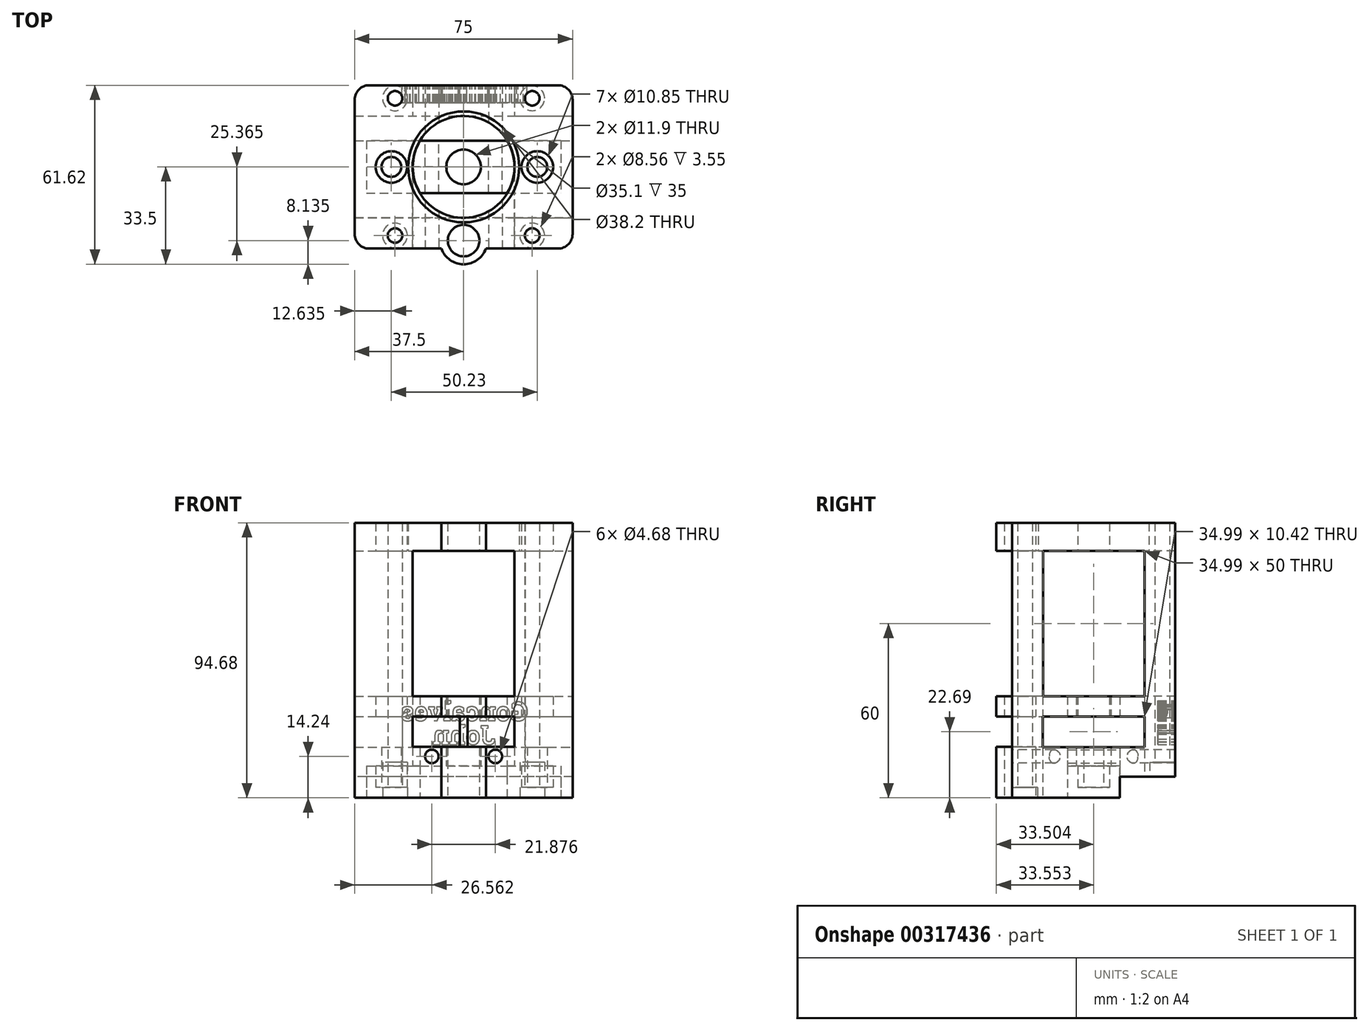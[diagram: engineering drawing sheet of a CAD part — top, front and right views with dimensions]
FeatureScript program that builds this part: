
annotation { "Feature Type Name" : "Feature", "Feature Type Description" : "" }
export const myFeature = defineFeature(function(context is Context, id is Id, definition is map)
    precondition{}
    {
        {
            var Q0;
            Q0=qCreatedBy(makeId("Top.planeOp"),FACE);
            var sketch = newSketch(context, id + "F0", { "sketchPlane" : qUnion([Q0])});
            skLineSegment(sketch, "E0.bottom", {"start": v(-33.5, 9.05) * mm, "end": v(33.5, 9.05) * mm});
            skLineSegment(sketch, "E0.top", {"start": v(-33.5, -9.05) * mm, "end": v(33.5, -9.05) * mm});
            skLineSegment(sketch, "E0.left", {"start": v(-33.5, 9.05) * mm, "end": v(-33.5, -9.05) * mm});
            skLineSegment(sketch, "E0.right", {"start": v(33.5, 9.05) * mm, "end": v(33.5, -9.05) * mm});
            skCircle(sketch, "E1", {"center": v(0, 0) * mm, "radius": 5.95 * mm});
            skCircle(sketch, "E2", {"center": v(25.37, 0) * mm, "radius": 3.42 * mm});
            skCircle(sketch, "E3", {"center": v(-24.87, 0) * mm, "radius": 3.42 * mm});
            skLineSegment(sketch, "E4.bottom", {"start": v(-14.98, 9.05) * mm, "end": v(14.98, 9.05) * mm});
            skLineSegment(sketch, "E4.top", {"start": v(-14.98, -9.05) * mm, "end": v(14.98, -9.05) * mm});
            skLineSegment(sketch, "E4.left", {"start": v(-14.98, 9.05) * mm, "end": v(-14.98, -9.05) * mm});
            skLineSegment(sketch, "E4.right", {"start": v(14.98, 9.05) * mm, "end": v(14.98, -9.05) * mm});
            skCircle(sketch, "E5", {"center": v(-24.87, 0) * mm, "radius": 5.42 * mm});
            skCircle(sketch, "E6", {"center": v(25.37, 0) * mm, "radius": 5.42 * mm});
            skCircle(sketch, "E7", {"center": v(0, 0) * mm, "radius": 17.5 * mm});
            skSolve(sketch);
        }
        {
            var Q0;
            Q0=makeQuery(id+"F0.imprint","IMPRINT",FACE,{"disambiguationData":[TD([[makeQuery(id+"F0.imprint","IMPRINT",EDGE,{"derivedFrom":sQuery(id+"F0.wireOp",EDGE,"E1")}),-1.0]])]});
            var Q1;
            {var subQ0=sQuery(id+"F0.wireOp",EDGE,"E4.left");Q1=makeQuery(id+"F0.imprint","IMPRINT",FACE,{"disambiguationData":[TD([[makeQuery(id+"F0.imprint","IMPRINT",EDGE,{"derivedFrom":subQ0}),-1.0]])]});}
            var Q2;
            {var subQ0=sQuery(id+"F0.wireOp",EDGE,"E4.right");Q2=makeQuery(id+"F0.imprint","IMPRINT",FACE,{"disambiguationData":[TD([[makeQuery(id+"F0.imprint","IMPRINT",EDGE,{"derivedFrom":subQ0}),1.0]])]});}
            extrude(context, id + "F1", {"entities" : qUnion([Q0, Q1, Q2]), "offsetDistance" : 25 * mm, "depth" : 28 * mm});
        }
        {
            var Q0;
            {var subQ1=sQuery(id+"F0.wireOp",EDGE,"E0.left");Q0=makeQuery(id+"F0.imprint","IMPRINT",FACE,{"disambiguationData":[TD([[makeQuery(id+"F0.imprint","IMPRINT",EDGE,{"derivedFrom":subQ1}),1.0]])]});}
            var Q1;
            {var subQ1=sQuery(id+"F0.wireOp",EDGE,"E0.right");Q1=makeQuery(id+"F0.imprint","IMPRINT",FACE,{"disambiguationData":[TD([[makeQuery(id+"F0.imprint","IMPRINT",EDGE,{"derivedFrom":subQ1}),-1.0]])]});}
            extrude(context, id + "F2", {"entities" : qUnion([Q0, Q1]), "operationType" : NewBodyOperationType.ADD, "offsetDistance" : 25 * mm, "depth" : 11 * mm});
        }
        {
            var Q0;
            Q0=makeQuery(id+"F0.imprint","IMPRINT",FACE,{"disambiguationData":[TD([[makeQuery(id+"F0.imprint","IMPRINT",EDGE,{"derivedFrom":sQuery(id+"F0.wireOp",EDGE,"E3")}),-1.0]])]});
            var Q1;
            Q1=makeQuery(id+"F0.imprint","IMPRINT",FACE,{"disambiguationData":[TD([[makeQuery(id+"F0.imprint","IMPRINT",EDGE,{"derivedFrom":sQuery(id+"F0.wireOp",EDGE,"E2")}),-1.0]])]});
            extrude(context, id + "F3", {"entities" : qUnion([Q0, Q1]), "operationType" : NewBodyOperationType.ADD, "offsetDistance" : 25 * mm, "depth" : 3.55 * mm});
        }
        {
            var Q0;
            {var subQ0=sQuery(id+"F0.wireOp",EDGE,"E4.top");Q0=makeQuery(id+"F0.imprint","IMPRINT",FACE,{"disambiguationData":[TD([[makeQuery(id+"F0.imprint","IMPRINT",EDGE,{"derivedFrom":subQ0}),-1.0]])]});}
            var Q1;
            Q1=makeQuery(id+"F0.imprint","IMPRINT",FACE,{"disambiguationData":[TD([[makeQuery(id+"F0.imprint","IMPRINT",EDGE,{"derivedFrom":sQuery(id+"F0.wireOp",EDGE,"E1")}),-1.0]])]});
            var Q2;
            {var subQ0=sQuery(id+"F0.wireOp",EDGE,"E4.right");Q2=makeQuery(id+"F0.imprint","IMPRINT",FACE,{"disambiguationData":[TD([[makeQuery(id+"F0.imprint","IMPRINT",EDGE,{"derivedFrom":subQ0}),1.0]])]});}
            var Q3;
            {var subQ0=sQuery(id+"F0.wireOp",EDGE,"E4.bottom");Q3=makeQuery(id+"F0.imprint","IMPRINT",FACE,{"disambiguationData":[TD([[makeQuery(id+"F0.imprint","IMPRINT",EDGE,{"derivedFrom":subQ0}),1.0]])]});}
            var Q4;
            {var subQ0=sQuery(id+"F0.wireOp",EDGE,"E4.left");Q4=makeQuery(id+"F0.imprint","IMPRINT",FACE,{"disambiguationData":[TD([[makeQuery(id+"F0.imprint","IMPRINT",EDGE,{"derivedFrom":subQ0}),-1.0]])]});}
            extrude(context, id + "F4", {"entities" : qUnion([Q0, Q1, Q2, Q3, Q4]), "operationType" : NewBodyOperationType.ADD, "offsetDistance" : 25 * mm, "depth" : 35 * mm, "hasSecondDirection" : true, "secondDirectionOppositeDirection" : false, "secondDirectionDepth" : 27.9 * mm});
        }
        {
            var Q0;
            Q0=qCreatedBy(makeId("Front.planeOp"),FACE);
            var sketch = newSketch(context, id + "F5", { "sketchPlane" : qUnion([Q0])});
            skLineSegment(sketch, "E8.bottom", {"start": v(-0.13, 35) * mm, "end": v(0.12, 35) * mm});
            skLineSegment(sketch, "E8.top", {"start": v(-0.12, 27.9) * mm, "end": v(0.13, 27.9) * mm});
            skLineSegment(sketch, "E8.left", {"start": v(-0.13, 35) * mm, "end": v(-0.12, 27.9) * mm});
            skLineSegment(sketch, "E8.right", {"start": v(0.12, 35) * mm, "end": v(0.13, 27.9) * mm});
            skSolve(sketch);
        }
        {
            var Q0;
            Q0=qSketchRegion(id+"F5",true);
            extrude(context, id + "F6", {"entities" : qUnion([Q0]), "operationType" : NewBodyOperationType.REMOVE, "oppositeDirection" : true, "offsetDistance" : 25 * mm, "depth" : 17.5 * mm, "hasSecondDirection" : true, "secondDirectionOppositeDirection" : true, "secondDirectionDepth" : 17.25 * mm});
        }
        {
            var Q0;
            {var subQ0=sQuery(id+"F0.wireOp",EDGE,"E4.bottom");var subQ1=sQuery(id+"F0.wireOp",EDGE,"E0.bottom");Q0=makeQuery(id+"FTeboLwCj6z0h2F_3.boolean.opBoolean","MERGE",FACE,{"derivedFrom":[makeQuery(id+"F2.opExtrude","SWEPT_FACE",FACE,{"disambiguationData":[OSD([subQ1]),TDD([makeQuery(id+"F0.imprint","IMPRINT",EDGE,{"disambiguationData":[TD([[makeQuery(id+"F0.imprint","INTERSECT",VERTEX,{"derivedFrom":[subQ1,sQuery(id+"F0.wireOp",EDGE,"E0.left")]}),-1.0]])],"derivedFrom":subQ1})])]}),makeQuery(id+"F2.opExtrude","SWEPT_FACE",FACE,{"disambiguationData":[OSD([subQ1]),TDD([makeQuery(id+"F0.imprint","IMPRINT",EDGE,{"disambiguationData":[TD([[makeQuery(id+"F0.imprint","INTERSECT",VERTEX,{"derivedFrom":[subQ1,sQuery(id+"F0.wireOp",EDGE,"E0.right")]}),1.0]])],"derivedFrom":subQ1})])]}),makeQuery(id+"F1.opExtrude","SWEPT_FACE",FACE,{"disambiguationData":[OSD([subQ0])]})]});}
            var sketch = newSketch(context, id + "F7", { "sketchPlane" : qUnion([Q0])});
            skCircle(sketch, "E9", {"center": v(-10.94, 14.24) * mm, "radius": 2.34 * mm});
            skCircle(sketch, "E10", {"center": v(10.94, 14.24) * mm, "radius": 2.34 * mm});
            skSolve(sketch);
        }
        {
            var Q0;
            Q0=makeQuery(id+"F7.imprint","IMPRINT",FACE,{"disambiguationData":[TD([[makeQuery(id+"F7.imprint","IMPRINT",EDGE,{"derivedFrom":sQuery(id+"F7.wireOp",EDGE,"E9")}),1.0]])]});
            var Q1;
            Q1=makeQuery(id+"F7.imprint","IMPRINT",FACE,{"disambiguationData":[TD([[makeQuery(id+"F7.imprint","IMPRINT",EDGE,{"derivedFrom":sQuery(id+"F7.wireOp",EDGE,"E10")}),1.0]])]});
            var Q2;
            Q2=sQuery(id+"F7.wireOp",EDGE,"E9");
            var Q3;
            Q3=sQuery(id+"F7.wireOp",EDGE,"E10");
            extrude(context, id + "F8", {"entities" : qUnion([Q0, Q1]), "operationType" : NewBodyOperationType.REMOVE, "surfaceEntities" : qUnion([Q2, Q3]), "endBound" : BoundingType.THROUGH_ALL, "oppositeDirection" : true, "offsetDistance" : 25 * mm, "depth" : 25 * mm});
        }
        {
            var Q0;
            Q0=qCreatedBy(makeId("Top.planeOp"),FACE);
            var sketch = newSketch(context, id + "F9", { "sketchPlane" : qUnion([Q0])});
            skLineSegment(sketch, "E11.rect.bottom", {"start": v(-32.5, 28.11) * mm, "end": v(32.5, 28.11) * mm});
            skLineSegment(sketch, "E11.rect.top", {"start": v(-32.5, -28.11) * mm, "end": v(32.5, -28.11) * mm});
            skLineSegment(sketch, "E11.rect.left", {"start": v(-37.5, 23.11) * mm, "end": v(-37.5, -23.11) * mm});
            skLineSegment(sketch, "E11.rect.right", {"start": v(37.5, 23.11) * mm, "end": v(37.5, -23.11) * mm});
            skPoint(sketch, "E11.rect.middle", {"position": v(0, 0) * mm});
            skCircle(sketch, "E12", {"center": v(0, 0) * mm, "radius": 19.1 * mm});
            skCircle(sketch, "E13", {"center": v(0, 0) * mm, "radius": 3.98 * mm});
            skCircle(sketch, "E14", {"center": v(-23.62, 23.62) * mm, "radius": 2.5 * mm});
            skCircle(sketch, "E15", {"center": v(23.62, 23.62) * mm, "radius": 2.5 * mm});
            skCircle(sketch, "E16", {"center": v(23.62, -23.62) * mm, "radius": 2.52 * mm});
            skCircle(sketch, "E17", {"center": v(-23.62, -23.62) * mm, "radius": 2.5 * mm});
            skLineSegment(sketch, "E18.rect.bottom", {"start": v(-23.62, 23.62) * mm, "end": v(23.62, 23.62) * mm, "construction": true});
            skLineSegment(sketch, "E18.rect.top", {"start": v(-23.62, -23.62) * mm, "end": v(23.62, -23.62) * mm, "construction": true});
            skLineSegment(sketch, "E18.rect.left", {"start": v(-23.62, 23.62) * mm, "end": v(-23.62, -23.62) * mm, "construction": true});
            skLineSegment(sketch, "E18.rect.right", {"start": v(23.62, 23.62) * mm, "end": v(23.62, -23.62) * mm, "construction": true});
            skCircle(sketch, "E19", {"center": v(0, 0) * mm, "radius": 5.38 * mm});
            skCircle(sketch, "E20", {"center": v(0, -25.37) * mm, "radius": 8.13 * mm});
            skCircle(sketch, "E21", {"center": v(-24.87, 0) * mm, "radius": 3.42 * mm});
            skCircle(sketch, "E22", {"center": v(25.36, 0) * mm, "radius": 3.41 * mm});
            skCircle(sketch, "E23", {"center": v(0, -25.37) * mm, "radius": 3.42 * mm});
            skPoint(sketch, "E24.visualSharp", {"position": v(-37.5, 28.11) * mm});
            skArc(sketch, "E24.filletArc", {"start": v(-32.5, 28.11) * mm, "mid": v(-36.04, 26.65) * mm, "end": v(-37.5, 23.11) * mm});
            skPoint(sketch, "E25.visualSharp", {"position": v(37.5, 28.11) * mm});
            skArc(sketch, "E25.filletArc", {"start": v(37.5, 23.11) * mm, "mid": v(36.04, 26.65) * mm, "end": v(32.5, 28.11) * mm});
            skPoint(sketch, "E26.visualSharp", {"position": v(37.5, -28.11) * mm});
            skArc(sketch, "E26.filletArc", {"start": v(32.5, -28.11) * mm, "mid": v(36.04, -26.65) * mm, "end": v(37.5, -23.11) * mm});
            skPoint(sketch, "E27.visualSharp", {"position": v(-37.5, -28.11) * mm});
            skArc(sketch, "E27.filletArc", {"start": v(-37.5, -23.11) * mm, "mid": v(-36.04, -26.65) * mm, "end": v(-32.5, -28.11) * mm});
            skCircle(sketch, "E28", {"center": v(0, 0) * mm, "radius": 17.55 * mm});
            skCircle(sketch, "E29", {"center": v(-24.87, 0) * mm, "radius": 5.42 * mm});
            skCircle(sketch, "E30", {"center": v(25.36, 0) * mm, "radius": 5.42 * mm});
            skCircle(sketch, "E31", {"center": v(0, -25.37) * mm, "radius": 5.42 * mm});
            skSolve(sketch);
        }
        {
            var Q0;
            Q0=qCreatedBy(makeId("Right.planeOp"),FACE);
            var sketch = newSketch(context, id + "F10", { "sketchPlane" : qUnion([Q0])});
            skLineSegment(sketch, "E32.bottom", {"start": v(-17.5, 27.9) * mm, "end": v(17.5, 27.9) * mm});
            skLineSegment(sketch, "E32.top", {"start": v(-17.5, 17.48) * mm, "end": v(17.5, 17.48) * mm});
            skLineSegment(sketch, "E32.left", {"start": v(-17.5, 27.9) * mm, "end": v(-17.5, 17.48) * mm});
            skLineSegment(sketch, "E32.right", {"start": v(17.5, 27.9) * mm, "end": v(17.5, 17.48) * mm});
            skLineSegment(sketch, "E33.bottom", {"start": v(-17.44, 85) * mm, "end": v(17.55, 85) * mm});
            skLineSegment(sketch, "E33.top", {"start": v(-17.5, 35) * mm, "end": v(17.55, 35) * mm});
            skLineSegment(sketch, "E33.left", {"start": v(-17.44, 85) * mm, "end": v(-17.44, 35) * mm});
            skLineSegment(sketch, "E33.right", {"start": v(17.55, 85) * mm, "end": v(17.55, 35) * mm});
            skSolve(sketch);
        }
        {
            var Q0;
            Q0=qCreatedBy(makeId("Front.planeOp"),FACE);
            var sketch = newSketch(context, id + "F11", { "sketchPlane" : qUnion([Q0])});
            skLineSegment(sketch, "E34.bottom", {"start": v(-17.55, 27.9) * mm, "end": v(17.44, 27.9) * mm});
            skLineSegment(sketch, "E34.top", {"start": v(-17.6, 17.48) * mm, "end": v(17.44, 17.48) * mm});
            skLineSegment(sketch, "E34.left", {"start": v(-17.55, 27.76) * mm, "end": v(-17.6, 17.34) * mm});
            skLineSegment(sketch, "E34.right", {"start": v(17.44, 27.76) * mm, "end": v(17.44, 17.34) * mm});
            skLineSegment(sketch, "E35.bottom", {"start": v(-17.5, 85) * mm, "end": v(17.5, 85) * mm});
            skLineSegment(sketch, "E35.top", {"start": v(-17.55, 35) * mm, "end": v(17.5, 35) * mm});
            skLineSegment(sketch, "E35.left", {"start": v(-17.5, 85) * mm, "end": v(-17.55, 35) * mm});
            skLineSegment(sketch, "E35.right", {"start": v(17.5, 85) * mm, "end": v(17.5, 35) * mm});
            skCircle(sketch, "E36", {"center": v(-10.94, 14.24) * mm, "radius": 2.34 * mm});
            skCircle(sketch, "E37", {"center": v(10.94, 14.24) * mm, "radius": 2.34 * mm});
            skSolve(sketch);
        }
        {
            var Q0;
            Q0=makeQuery(id+"F9.imprint","IMPRINT",FACE,{"disambiguationData":[TD([[makeQuery(id+"F9.imprint","IMPRINT",EDGE,{"derivedFrom":sQuery(id+"F9.wireOp",EDGE,"E11.rect.bottom")}),-1.0]])]});
            var Q1;
            {var subQ0=sQuery(id+"F9.wireOp",EDGE,"E20");var subQ1=sQuery(id+"F9.wireOp",EDGE,"E11.rect.top");var subQ2=makeQuery(id+"F9.imprint","INTERSECT",VERTEX,{"disambiguationData":[OD(0.0)],"derivedFrom":[subQ1,subQ0]});Q1=makeQuery(id+"F9.imprint","IMPRINT",FACE,{"disambiguationData":[TD([[makeQuery(id+"F9.imprint","IMPRINT",EDGE,{"disambiguationData":[TD([[subQ2,-1.0]])],"derivedFrom":subQ1}),-1.0]])]});}
            var Q2;
            {var subQ0=sQuery(id+"F9.wireOp",EDGE,"E20");var subQ4=sQuery(id+"F9.wireOp",EDGE,"E11.rect.top");var subQ5=makeQuery(id+"F9.imprint","INTERSECT",VERTEX,{"disambiguationData":[OD(0.0)],"derivedFrom":[subQ4,subQ0]});Q2=makeQuery(id+"F9.imprint","IMPRINT",FACE,{"disambiguationData":[TD([[makeQuery(id+"F9.imprint","IMPRINT",EDGE,{"disambiguationData":[TD([[subQ5,-1.0]])],"derivedFrom":subQ4}),1.0]])]});}
            extrude(context, id + "F12", {"entities" : qUnion([Q0, Q1, Q2]), "depth" : 94.68 * mm, "offsetDistance" : 25 * mm});
        }
        {
            var Q0;
            {var subQ0=sQuery(id+"F9.wireOp",EDGE,"E20");var subQ1=sQuery(id+"F9.wireOp",EDGE,"E12");var subQ2=makeQuery(id+"F9.imprint","INTERSECT",VERTEX,{"disambiguationData":[OD(0.0)],"derivedFrom":[subQ1,subQ0]});Q0=makeQuery(id+"F9.imprint","IMPRINT",FACE,{"disambiguationData":[TD([[makeQuery(id+"F9.imprint","IMPRINT",EDGE,{"disambiguationData":[TD([[subQ2,-1.0]])],"derivedFrom":subQ1}),1.0]])]});}
            var Q1;
            {var subQ0=sQuery(id+"F9.wireOp",EDGE,"E20");var subQ1=sQuery(id+"F9.wireOp",EDGE,"E12");var subQ2=makeQuery(id+"F9.imprint","INTERSECT",VERTEX,{"disambiguationData":[OD(0.0)],"derivedFrom":[subQ1,subQ0]});Q1=makeQuery(id+"F9.imprint","IMPRINT",FACE,{"disambiguationData":[TD([[makeQuery(id+"F9.imprint","IMPRINT",EDGE,{"disambiguationData":[TD([[subQ2,1.0]])],"derivedFrom":subQ1}),1.0]])]});}
            var Q2;
            Q2=makeQuery(id+"F4.opExtrude","CAP_FACE",FACE,{"disambiguationData":[OSD([sQuery(id+"F0.wireOp",EDGE,"E1"),sQuery(id+"F0.wireOp",EDGE,"E7")])],"isStart":false});
            extrude(context, id + "F13", {"entities" : qUnion([Q0, Q1]), "operationType" : NewBodyOperationType.ADD, "depth" : 35 * mm, "endBoundEntityFace" : qUnion([Q2]), "offsetDistance" : 25 * mm});
        }
        {
            var Q0;
            Q0 = qSketchRegion(id + "F10", true);
            var Q1;
            Q1=makeQuery(id+"F12.opExtrude","SWEPT_FACE",FACE,{"disambiguationData":[OSD([sQuery(id+"F9.wireOp",EDGE,"E11.rect.left")])]});
            var Q2;
            Q2=makeQuery(id+"F12.opExtrude","SWEPT_FACE",FACE,{"disambiguationData":[OSD([sQuery(id+"F9.wireOp",EDGE,"E11.rect.right")])]});
            extrude(context, id + "F14", {"entities" : qUnion([Q0]), "operationType" : NewBodyOperationType.REMOVE, "endBound" : BoundingType.UP_TO_SURFACE, "oppositeDirection" : true, "depth" : 25 * mm, "endBoundEntityFace" : qUnion([Q1]), "offsetDistance" : 25 * mm, "hasSecondDirection" : true, "secondDirectionBound" : SecondDirectionBoundingType.UP_TO_SURFACE, "secondDirectionOppositeDirection" : false, "secondDirectionDepth" : 25 * mm, "secondDirectionBoundEntityFace" : qUnion([Q2])});
        }
        {
            var Q0;
            Q0 = qSketchRegion(id + "F11", true);
            var Q1;
            Q1=makeQuery(id+"F12.opExtrude","SWEPT_FACE",FACE,{"disambiguationData":[OSD([sQuery(id+"F9.wireOp",EDGE,"E11.rect.bottom")])]});
            var Q2;
            {var subQ0=sQuery(id+"F9.wireOp",EDGE,"E11.rect.top");Q2=makeQuery(id+"F12.opExtrude","SWEPT_FACE",FACE,{"disambiguationData":[OSD([subQ0]),TDD([makeQuery(id+"F9.imprint","IMPRINT",EDGE,{"disambiguationData":[TD([[makeQuery(id+"F9.imprint","INTERSECT",VERTEX,{"derivedFrom":[subQ0,sQuery(id+"F9.wireOp",EDGE,"E27.filletArc")]}),-1.0]])],"derivedFrom":subQ0})])]});}
            extrude(context, id + "F15", {"entities" : qUnion([Q0]), "operationType" : NewBodyOperationType.REMOVE, "endBound" : BoundingType.UP_TO_SURFACE, "oppositeDirection" : true, "depth" : 25 * mm, "endBoundEntityFace" : qUnion([Q1]), "offsetDistance" : 25 * mm, "hasSecondDirection" : true, "secondDirectionOppositeDirection" : false, "secondDirectionDepth" : 35 * mm, "secondDirectionBoundEntityFace" : qUnion([Q2])});
        }
        {
            var Q0;
            Q0=qCreatedBy(makeId("Front.planeOp"),FACE);
            var sketch = newSketch(context, id + "F16", { "sketchPlane" : qUnion([Q0])});
            skLineSegment(sketch, "E38.bottom", {"start": v(-17.55, 27.94) * mm, "end": v(17.44, 27.94) * mm});
            skLineSegment(sketch, "E38.top", {"start": v(-17.6, 17.52) * mm, "end": v(17.44, 17.52) * mm});
            skLineSegment(sketch, "E38.left", {"start": v(-17.55, 27.94) * mm, "end": v(-17.6, 17.52) * mm});
            skLineSegment(sketch, "E38.right", {"start": v(17.44, 27.94) * mm, "end": v(17.44, 17.52) * mm});
            skSolve(sketch);
        }
        {
            var Q0;
            Q0 = qSketchRegion(id + "F16", true);
            extrude(context, id + "F17", {"entities" : qUnion([Q0]), "operationType" : NewBodyOperationType.REMOVE, "depth" : 34 * mm, "offsetDistance" : 25 * mm});
        }
        {
            var Q0;
            {var subQ0=sQuery(id+"F9.wireOp",EDGE,"E31");var subQ1=sQuery(id+"F9.wireOp",EDGE,"E11.rect.top");var subQ2=makeQuery(id+"F9.imprint","INTERSECT",VERTEX,{"disambiguationData":[OD(0.0)],"derivedFrom":[subQ1,subQ0]});Q0=makeQuery(id+"F9.imprint","IMPRINT",FACE,{"disambiguationData":[TD([[makeQuery(id+"F9.imprint","IMPRINT",EDGE,{"disambiguationData":[TD([[subQ2,-1.0]])],"derivedFrom":subQ1}),-1.0]])]});}
            var Q1;
            {var subQ0=sQuery(id+"F9.wireOp",EDGE,"E31");var subQ1=sQuery(id+"F9.wireOp",EDGE,"E11.rect.top");var subQ2=makeQuery(id+"F9.imprint","INTERSECT",VERTEX,{"disambiguationData":[OD(0.0)],"derivedFrom":[subQ1,subQ0]});Q1=makeQuery(id+"F9.imprint","IMPRINT",FACE,{"disambiguationData":[TD([[makeQuery(id+"F9.imprint","IMPRINT",EDGE,{"disambiguationData":[TD([[subQ2,-1.0]])],"derivedFrom":subQ1}),1.0]])]});}
            var Q2;
            Q2=makeQuery(id+"F17.boolean.opBoolean","COPY",FACE,{"derivedFrom":makeQuery(id+"F17.opExtrude","SWEPT_FACE",FACE,{"disambiguationData":[OSD([sQuery(id+"F16.wireOp",EDGE,"E38.top")])]})});
            extrude(context, id + "F18", {"entities" : qUnion([Q0, Q1]), "operationType" : NewBodyOperationType.ADD, "endBound" : BoundingType.UP_TO_SURFACE, "depth" : 17.48 * mm, "endBoundEntityFace" : qUnion([Q2]), "offsetDistance" : 25 * mm});
        }
        {
            var Q0;
            Q0=qCreatedBy(makeId("Top.planeOp"),FACE);
            var sketch = newSketch(context, id + "F19", { "sketchPlane" : qUnion([Q0])});
            skLineSegment(sketch, "E39.bottom", {"start": v(-33.5, 9.04) * mm, "end": v(33.5, 9.04) * mm});
            skLineSegment(sketch, "E39.top", {"start": v(-33.5, -9.06) * mm, "end": v(33.5, -9.06) * mm});
            skLineSegment(sketch, "E39.left", {"start": v(-33.5, 9.04) * mm, "end": v(-33.5, -9.06) * mm});
            skLineSegment(sketch, "E39.right", {"start": v(33.5, 9.04) * mm, "end": v(33.5, -9.06) * mm});
            skLineSegment(sketch, "E40.bottom", {"start": v(-14.97, 9.04) * mm, "end": v(14.99, 9.04) * mm});
            skLineSegment(sketch, "E40.top", {"start": v(-14.97, -9.06) * mm, "end": v(14.99, -9.06) * mm});
            skSolve(sketch);
        }
        {
            var Q0;
            Q0 = qSketchRegion(id + "F19", true);
            extrude(context, id + "F20", {"entities" : qUnion([Q0]), "operationType" : NewBodyOperationType.REMOVE, "depth" : 11 * mm, "offsetDistance" : 25 * mm});
        }
        {
            var Q0;
            Q0=makeQuery(id+"F9.imprint","IMPRINT",FACE,{"disambiguationData":[TD([[makeQuery(id+"F9.imprint","IMPRINT",EDGE,{"derivedFrom":sQuery(id+"F9.wireOp",EDGE,"E21")}),-1.0]])]});
            var Q1;
            Q1=makeQuery(id+"F9.imprint","IMPRINT",FACE,{"disambiguationData":[TD([[makeQuery(id+"F9.imprint","IMPRINT",EDGE,{"derivedFrom":sQuery(id+"F9.wireOp",EDGE,"E22")}),-1.0]])]});
            var Q2;
            Q2=makeQuery(id+"F14.boolean.opBoolean","COPY",FACE,{"disambiguationData":[TD([makeQuery(id+"F12.opExtrude","SWEPT_FACE",FACE,{"disambiguationData":[OSD([sQuery(id+"F9.wireOp",EDGE,"E11.rect.left")])]})])],"derivedFrom":makeQuery(id+"F14.opExtrude","SWEPT_FACE",FACE,{"disambiguationData":[OSD([sQuery(id+"F10.wireOp",EDGE,"E32.top")])]})});
            var Q3;
            Q3=makeQuery(id+"F14.boolean.opBoolean","COPY",FACE,{"disambiguationData":[TD([makeQuery(id+"F12.opExtrude","SWEPT_FACE",FACE,{"disambiguationData":[OSD([sQuery(id+"F9.wireOp",EDGE,"E11.rect.left")])]})])],"derivedFrom":makeQuery(id+"F14.opExtrude","SWEPT_FACE",FACE,{"disambiguationData":[OSD([sQuery(id+"F10.wireOp",EDGE,"E32.top")])]})});
            extrude(context, id + "F21", {"entities" : qUnion([Q0, Q1]), "operationType" : NewBodyOperationType.ADD, "endBound" : BoundingType.UP_TO_SURFACE, "depth" : 3.6 * mm, "endBoundEntityFace" : qUnion([Q2]), "offsetDistance" : 25 * mm, "hasSecondDirection" : true, "secondDirectionOppositeDirection" : false, "secondDirectionDepth" : 3.6 * mm, "secondDirectionBoundEntityFace" : qUnion([Q3])});
        }
        {
            var Q0;
            Q0=qCreatedBy(makeId("Top.planeOp"),FACE);
            var sketch = newSketch(context, id + "F22", { "sketchPlane" : qUnion([Q0])});
            skCircle(sketch, "E41", {"center": v(-23.62, -23.62) * mm, "radius": 4.28 * mm});
            skCircle(sketch, "E42", {"center": v(23.62, -23.62) * mm, "radius": 4.28 * mm});
            skSolve(sketch);
        }
        {
            var Q0;
            Q0 = qSketchRegion(id + "F22", true);
            extrude(context, id + "F23", {"entities" : qUnion([Q0]), "operationType" : NewBodyOperationType.REMOVE, "depth" : 3.55 * mm, "offsetDistance" : 25 * mm});
        }
        {
            var Q0;
            Q0=qCreatedBy(makeId("Top.planeOp"),FACE);
            var sketch = newSketch(context, id + "F24", { "sketchPlane" : qUnion([Q0])});
            skCircle(sketch, "E43", {"center": v(-23.62, 23.62) * mm, "radius": 4.28 * mm});
            skCircle(sketch, "E44", {"center": v(23.62, 23.62) * mm, "radius": 4.27 * mm});
            skSolve(sketch);
        }
        {
            var Q0;
            Q0 = qSketchRegion(id + "F24", true);
            extrude(context, id + "F25", {"entities" : qUnion([Q0]), "operationType" : NewBodyOperationType.REMOVE, "depth" : 12.27 * mm, "offsetDistance" : 25 * mm, "hasSecondDirection" : true, "secondDirectionOppositeDirection" : false, "secondDirectionDepth" : 7.25 * mm});
        }
        {
            var Q0;
            Q0=qCreatedBy(makeId("Top.planeOp"),FACE);
            var sketch = newSketch(context, id + "F26", { "sketchPlane" : qUnion([Q0])});
            skLineSegment(sketch, "E45.bottom", {"start": v(37.5, 28.12) * mm, "end": v(-37.5, 28.11) * mm});
            skLineSegment(sketch, "E45.top", {"start": v(37.5, 9.05) * mm, "end": v(-37.5, 9.05) * mm});
            skLineSegment(sketch, "E45.left", {"start": v(37.5, 28.12) * mm, "end": v(37.5, 9.05) * mm});
            skLineSegment(sketch, "E45.right", {"start": v(-37.5, 28.11) * mm, "end": v(-37.5, 9.05) * mm});
            skSolve(sketch);
        }
        {
            var Q0;
            Q0 = qSketchRegion(id + "F26", true);
            extrude(context, id + "F27", {"entities" : qUnion([Q0]), "operationType" : NewBodyOperationType.REMOVE, "depth" : 7.25 * mm, "offsetDistance" : 25 * mm});
        }
        {
            var Q0;
            Q0=makeQuery(id+"F12.opExtrude","SWEPT_FACE",FACE,{"disambiguationData":[OSD([sQuery(id+"F9.wireOp",EDGE,"E11.rect.bottom")])]});
            var sketch = newSketch(context, id + "F28", { "sketchPlane" : qUnion([Q0])});
            skText(sketch, "E46", { "text": "John", "fontName": "RobotoSlab-Bold.ttf"});
            skText(sketch, "E47", { "text": "Goncalves", "fontName": "RobotoSlab-Bold.ttf"});
            const initialGuessF28  = {"E46": [-0.01097, 0.01837, 1, 0, 0.00645], "E47": [-0.02204, 0.02654, 1, 0, 0.00645]};
            skSetInitialGuess(sketch, initialGuessF28);
            skSolve(sketch);
        }
        {
            var Q0;
            Q0 = qSketchRegion(id + "F28", true);
            var Q1;
            Q1=makeQuery(id+"F14.boolean.opBoolean","COPY",FACE,{"disambiguationData":[TD([makeQuery(id+"F12.opExtrude","SWEPT_FACE",FACE,{"disambiguationData":[OSD([sQuery(id+"F9.wireOp",EDGE,"E11.rect.left")])]})])],"derivedFrom":makeQuery(id+"F14.opExtrude","SWEPT_FACE",FACE,{"disambiguationData":[OSD([sQuery(id+"F10.wireOp",EDGE,"E32.right")])]})});
            extrude(context, id + "F29", {"entities" : qUnion([Q0]), "operationType" : NewBodyOperationType.REMOVE, "oppositeDirection" : true, "depth" : 6 * mm, "endBoundEntityFace" : qUnion([Q1]), "offsetDistance" : 25 * mm});
        }
    });
